# Revit family: oventrop_hydrocontrol-vfc-pn16_1062951-55rfa
name_source: partatom
category: Арматура трубопроводов
revit_build: Autodesk Revit 2017 (Build: 20160225_1515(x64)
units: mm (PartAtom-declared; Revit-internal decimal feet)

## family parameters
Всегда вертикально = Да
Заголовок OmniClass = Adjusting/Controlling Valves for Liquid Services
На основе рабочей плоскости = Нет
Номер OmniClass = 23.65.55.14.17
Общий = Нет
При загрузке вырезать с полостями = Нет
Размер круглого соединителя = Использовать радиус
Тип детали = Клапан - Вставляется

## types (5) — shared parameters
Angle = 60.00°
Angle 2 = 30.00°
Angle 3 = -60.00°
Article Description = Balancing valve with flanges, ANSI 150
Article Type = Hydrocontrol VFC 10629 DN 65-150 PN16 ANSI
Black = Color RGB 35-35-35
Bronze = Color RGB 156-122-90
Custom = Нет
EMCS Version = 2.0
ETIM Article Class = EC011463
Family Version = 10.14
Hb4 = 18 мм
Hb5 = 3 мм
Hlp1 = 22 мм
IFCExportAs = IfcValveType
IFCExportType = PRESSUREREDUCING
Lgt1 = 2 мм
MEPcontent Class = VALVE_BALANCING
Manufacturer URL = http://www.oventrop.de
Pressure Drop = 0.0 Па
Product Line = Oventrop
R1 = 9 мм
R2 = 10 мм
Revit Version = 2015
Steel = Color RGB 140-140-140
r1 = 2 мм
r2 = 3 мм
Группа модели = Hydrocontrol VFC 10629 DN 65-150 PN16 ANSI
Изготовитель = Oventrop
Описание = Balancing valve with flanges, ANSI 150

## per-type parameters (varying)
- DN 65: CurDst=23 мм; Dst1=12 мм; DstChk=12 мм; FlangeDiameter=185 мм; GTIN=4026755179415; H=191 мм; Hb1=188 мм; Hb2=75 мм; Hb3=19 мм; Hb6=80 мм; Height=188 мм; Hlp2=8 мм; K=140 мм; L2=23 мм; Length=290 мм; Lgt2=16 мм; Lgt3=34 мм; Lgt4=110 мм; Manufacturer Art. No.=1062951; NominalDiameter=65 мм; NominalRadius=33 мм; OuterDiameter=76 мм; Rad1=70 мм; Rad2=93 мм; Rad3=43 мм; Rad4=40 мм; Rad5=43 мм; Rad6=33 мм; Rad7=45 мм; RegulatorRadius=55 мм; URL=www.stabiplan.com; VDst=29 мм; VHth=50 мм
- DN 80: CurDst=28 мм; Dst1=13 мм; DstChk=13 мм; FlangeDiameter=200 мм; GTIN=4026755179422; H=206 мм; Hb1=206 мм; Hb2=88 мм; Hb3=22 мм; Hb6=95 мм; Height=203 мм; Hlp2=9 мм; K=152 мм; L2=28 мм; Length=310 мм; Lgt2=16 мм; Lgt3=37 мм; Lgt4=110 мм; Manufacturer Art. No.=1062952; NominalDiameter=80 мм; NominalRadius=40 мм; OuterDiameter=89 мм; Rad1=76 мм; Rad2=100 мм; Rad3=52 мм; Rad4=49 мм; Rad5=51 мм; Rad6=41 мм; Rad7=53 мм; RegulatorRadius=55 мм; URL=www.stabiplan.com; VDst=32 мм; VHth=59 мм
- DN 100: CurDst=34 мм; Dst1=11 мм; DstChk=11 мм; FlangeDiameter=220 мм; GTIN=4026755179439; H=243 мм; Hb1=234 мм; Hb2=110 мм; Hb3=27 мм; Hb6=120 мм; Height=240 мм; Hlp2=11 мм; K=191 мм; L2=34 мм; Length=350 мм; Lgt2=17 мм; Lgt3=41 мм; Lgt4=110 мм; Manufacturer Art. No.=1062953; NominalDiameter=100 мм; NominalRadius=50 мм; OuterDiameter=114 мм; Rad1=96 мм; Rad2=110 мм; Rad3=62 мм; Rad4=59 мм; Rad5=62 мм; Rad6=52 мм; Rad7=64 мм; RegulatorRadius=80 мм; URL=http://file-system.ru; VDst=36 мм; VHth=69 мм
- DN 125: CurDst=42 мм; Dst1=0 мм; DstChk=0 мм; FlangeDiameter=250 мм; GTIN=4026755179446; H=286 мм; Hb1=284 мм; Hb2=152 мм; Hb3=38 мм; Hb6=169 мм; Height=283 мм; Hlp2=14 мм; K=216 мм; L2=42 мм; Length=400 мм; Lgt2=18 мм; Lgt3=45 мм; Lgt4=158 мм; Manufacturer Art. No.=1062954; NominalDiameter=125 мм; NominalRadius=63 мм; OuterDiameter=140 мм; Rad1=108 мм; Rad2=125 мм; Rad3=76 мм; Rad4=73 мм; Rad5=75 мм; Rad6=65 мм; Rad7=77 мм; RegulatorRadius=80 мм; URL=www.stabiplan.com; VDst=40 мм; VHth=83 мм
- DN 150: CurDst=50 мм; Dst1=17 мм; DstChk=17 мм; FlangeDiameter=285 мм; GTIN=4026755179453; H=288 мм; Hb1=286 мм; Hb2=146 мм; Hb3=37 мм; Hb6=162 мм; Height=285 мм; Hlp2=17 мм; K=241 мм; L2=50 мм; Length=480 мм; Lgt2=18 мм; Lgt3=50 мм; Lgt4=205 мм; Manufacturer Art. No.=1062955; NominalDiameter=150 мм; NominalRadius=75 мм; OuterDiameter=168 мм; Rad1=121 мм; Rad2=143 мм; Rad3=89 мм; Rad4=86 мм; Rad5=89 мм; Rad6=79 мм; Rad7=91 мм; RegulatorRadius=80 мм; URL=www.stabiplan.com; VDst=45 мм; VHth=96 мм

## geometry (parser evidence)
native form markers: Blend x2, Sweep x2
no freeform markers — native parametric forms only
